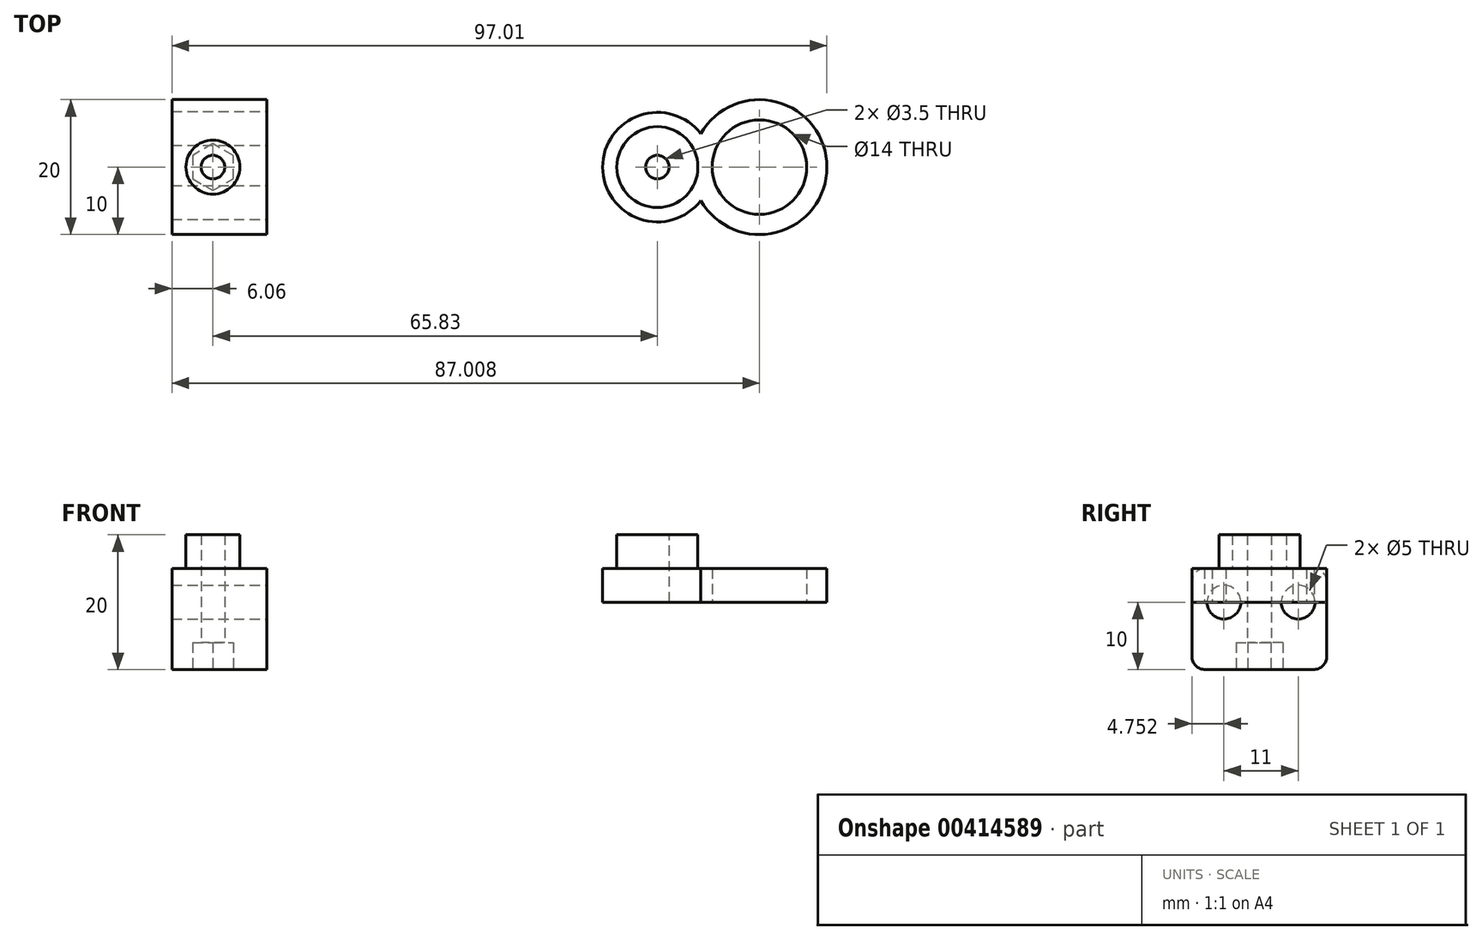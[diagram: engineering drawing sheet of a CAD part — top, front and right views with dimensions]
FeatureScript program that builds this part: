
annotation { "Feature Type Name" : "Feature", "Feature Type Description" : "" }
export const myFeature = defineFeature(function(context is Context, id is Id, definition is map)
    precondition{}
    {
        {
            var Q0;
            Q0=qCreatedBy(makeId("Top.planeOp"),FACE);
            var sketch = newSketch(context, id + "F0", { "sketchPlane" : qUnion([Q0])});
            skCircle(sketch, "E0", {"center": v(15.12, 0) * mm, "radius": 7 * mm});
            skArc(sketch, "E1", {"start": v(6.43, 4.95) * mm, "mid": v(-8.12, 0) * mm, "end": v(6.43, -4.95) * mm});
            skArc(sketch, "E2", {"start": v(6.43, -4.95) * mm, "mid": v(25.12, 0) * mm, "end": v(6.43, 4.95) * mm});
            skCircle(sketch, "E3", {"center": v(0, 0) * mm, "radius": 6 * mm});
            skSolve(sketch);
        }
        {
            var Q0;
            Q0=makeQuery(id+"F0.imprint","IMPRINT",FACE,{"disambiguationData":[TD([[makeQuery(id+"F0.imprint","IMPRINT",EDGE,{"derivedFrom":sQuery(id+"F0.wireOp",EDGE,"E0")}),-1.0]])]});
            extrude(context, id + "F1", {"entities" : qUnion([Q0]), "depth" : 5 * mm});
        }
        {
            var Q0;
            Q0=makeQuery(id+"F0.imprint","IMPRINT",FACE,{"disambiguationData":[TD([[makeQuery(id+"F0.imprint","IMPRINT",EDGE,{"derivedFrom":sQuery(id+"F0.wireOp",EDGE,"E3")}),1.0]])]});
            extrude(context, id + "F2", {"entities" : qUnion([Q0]), "operationType" : NewBodyOperationType.ADD, "depth" : 10 * mm});
        }
        {
            var Q0;
            Q0=makeQuery(id+"F2.opExtrude","CAP_FACE",FACE,{"disambiguationData":[OSD([sQuery(id+"F0.wireOp",EDGE,"E3")])],"isStart":false});
            var sketch = newSketch(context, id + "F3", { "sketchPlane" : qUnion([Q0])});
            skCircle(sketch, "E4", {"center": v(0, 0) * mm, "radius": 1.75 * mm});
            skSolve(sketch);
        }
        {
            var Q0;
            Q0=makeQuery(id+"F3.imprint","IMPRINT",FACE,{"disambiguationData":[TD([[makeQuery(id+"F3.imprint","IMPRINT",EDGE,{"derivedFrom":sQuery(id+"F3.wireOp",EDGE,"E4")}),1.0]])]});
            extrude(context, id + "F4", {"entities" : qUnion([Q0]), "operationType" : NewBodyOperationType.REMOVE, "oppositeDirection" : true, "depth" : 25 * mm});
        }
        {
            var Q0;
            Q0=qCreatedBy(makeId("Top.planeOp"),FACE);
            var sketch = newSketch(context, id + "F5", { "sketchPlane" : qUnion([Q0])});
            skCircle(sketch, "E5", {"center": v(-65.83, 0) * mm, "radius": 1.75 * mm});
            skCircle(sketch, "E6", {"center": v(-65.83, 0) * mm, "radius": 6 * mm});
            skLineSegment(sketch, "E7.bottom", {"start": v(-57.83, 10) * mm, "end": v(-60.83, 10) * mm});
            skLineSegment(sketch, "E7.top", {"start": v(-57.83, -10) * mm, "end": v(-60.83, -10) * mm});
            skLineSegment(sketch, "E7.left", {"start": v(-57.83, 10) * mm, "end": v(-57.83, -10) * mm});
            skLineSegment(sketch, "E7.right", {"start": v(-60.83, 10) * mm, "end": v(-60.83, 3.32) * mm});
            skCircle(sketch, "E8", {"center": v(-65.83, 0) * mm, "radius": 4 * mm});
            skLineSegment(sketch, "E9.trimOffspring", {"start": v(-60.83, -3.32) * mm, "end": v(-60.83, -10) * mm});
            skLineSegment(sketch, "E10.bottom", {"start": v(-60.83, 10) * mm, "end": v(-71.9, 10) * mm});
            skLineSegment(sketch, "E10.top", {"start": v(-60.83, -10) * mm, "end": v(-71.9, -10) * mm});
            skLineSegment(sketch, "E10.left", {"start": v(-60.83, 10) * mm, "end": v(-60.83, -10) * mm});
            skLineSegment(sketch, "E10.right", {"start": v(-71.9, 10) * mm, "end": v(-71.9, -10) * mm});
            skSolve(sketch);
        }
        {
            var Q0;
            Q0=makeQuery(id+"F5.imprint","IMPRINT",FACE,{"disambiguationData":[TD([[makeQuery(id+"F5.imprint","IMPRINT",EDGE,{"derivedFrom":sQuery(id+"F5.wireOp",EDGE,"E6")}),1.0]])]});
            var Q1;
            Q1=makeQuery(id+"F5.imprint","IMPRINT",FACE,{"disambiguationData":[TD([[makeQuery(id+"F5.imprint","IMPRINT",EDGE,{"derivedFrom":sQuery(id+"F5.wireOp",EDGE,"E8")}),-1.0]])]});
            extrude(context, id + "F6", {"entities" : qUnion([Q0, Q1]), "depth" : 5 * mm, "offsetDistance" : 25 * mm, "hasSecondDirection" : true, "secondDirectionOppositeDirection" : true, "secondDirectionDepth" : 10 * mm});
        }
        {
            var Q0;
            Q0=makeQuery(id+"F5.imprint","IMPRINT",FACE,{"disambiguationData":[TD([[makeQuery(id+"F5.imprint","IMPRINT",EDGE,{"derivedFrom":sQuery(id+"F5.wireOp",EDGE,"E5")}),-1.0]])]});
            extrude(context, id + "F7", {"entities" : qUnion([Q0]), "operationType" : NewBodyOperationType.ADD, "depth" : 10 * mm, "offsetDistance" : 25 * mm, "hasSecondDirection" : true, "secondDirectionOppositeDirection" : true, "secondDirectionDepth" : 10 * mm});
        }
        {
            var Q0;
            {var subQ1=sQuery(id+"F5.wireOp",EDGE,"E7.bottom");Q0=makeQuery(id+"F5.imprint","IMPRINT",FACE,{"disambiguationData":[TD([[makeQuery(id+"F5.imprint","IMPRINT",EDGE,{"derivedFrom":subQ1}),1.0]])]});}
            var Q1;
            {var subQ1=sQuery(id+"F5.wireOp",EDGE,"E10.bottom");Q1=makeQuery(id+"F5.imprint","IMPRINT",FACE,{"disambiguationData":[TD([[makeQuery(id+"F5.imprint","IMPRINT",EDGE,{"derivedFrom":subQ1}),1.0]])]});}
            extrude(context, id + "F8", {"entities" : qUnion([Q0, Q1]), "operationType" : NewBodyOperationType.ADD, "depth" : 5 * mm, "offsetDistance" : 25 * mm, "hasSecondDirection" : true, "secondDirectionOppositeDirection" : true, "secondDirectionDepth" : 10 * mm});
        }
        {
            var Q0;
            Q0=makeQuery(id+"F8.opExtrude","SWEPT_FACE",FACE,{"disambiguationData":[OSD([sQuery(id+"F5.wireOp",EDGE,"E7.left")])]});
            var sketch = newSketch(context, id + "F9", { "sketchPlane" : qUnion([Q0])});
            skCircle(sketch, "E11", {"center": v(-5.25, 0) * mm, "radius": 2.5 * mm});
            skCircle(sketch, "E12", {"center": v(5.75, 0) * mm, "radius": 2.5 * mm});
            skSolve(sketch);
        }
        {
            var Q0;
            Q0=makeQuery(id+"F9.imprint","IMPRINT",FACE,{"disambiguationData":[TD([[makeQuery(id+"F9.imprint","IMPRINT",EDGE,{"derivedFrom":sQuery(id+"F9.wireOp",EDGE,"E11")}),1.0]])]});
            var Q1;
            Q1=makeQuery(id+"F9.imprint","IMPRINT",FACE,{"disambiguationData":[TD([[makeQuery(id+"F9.imprint","IMPRINT",EDGE,{"derivedFrom":sQuery(id+"F9.wireOp",EDGE,"E12")}),1.0]])]});
            extrude(context, id + "F10", {"entities" : qUnion([Q0, Q1]), "operationType" : NewBodyOperationType.REMOVE, "oppositeDirection" : true, "depth" : 20 * mm, "offsetDistance" : 25 * mm});
        }
        {
            var Q0;
            Q0=makeQuery(id+"F8.opExtrude","CAP_EDGE",EDGE,{"disambiguationData":[OSD([sQuery(id+"F5.wireOp",EDGE,"E7.top")])],"isStart":false});
            var Q1;
            Q1=makeQuery(id+"F8.opExtrude","CAP_EDGE",EDGE,{"disambiguationData":[OSD([sQuery(id+"F5.wireOp",EDGE,"E7.top")])],"isStart":true});
            var Q2;
            Q2=makeQuery(id+"F8.opExtrude","CAP_EDGE",EDGE,{"disambiguationData":[OSD([sQuery(id+"F5.wireOp",EDGE,"E7.bottom")])],"isStart":false});
            var Q3;
            Q3=makeQuery(id+"F8.opExtrude","CAP_EDGE",EDGE,{"disambiguationData":[OSD([sQuery(id+"F5.wireOp",EDGE,"E7.bottom")])],"isStart":true});
            fillet(context, id + "F11", {"entities" : qUnion([Q0, Q1, Q2, Q3]), "radius" : 2 * mm, "tangentPropagation" : true, "allowEdgeOverflow" : false});
        }
        {
            var Q0;
            {var subQ0=sQuery(id+"F5.wireOp",EDGE,"E6");var subQ1=sQuery(id+"F5.wireOp",EDGE,"E8");Q0=makeQuery(id+"F8.boolean.opBoolean","MERGE",FACE,{"derivedFrom":[makeQuery(id+"F7.boolean.opBoolean","MERGE",FACE,{"derivedFrom":[makeQuery(id+"F6.opExtrude","CAP_FACE",FACE,{"disambiguationData":[OSD([subQ0,subQ1])],"isStart":true}),makeQuery(id+"F7.opExtrude","CAP_FACE",FACE,{"disambiguationData":[OSD([sQuery(id+"F5.wireOp",EDGE,"E5"),subQ1])],"isStart":true})]}),makeQuery(id+"F8.opExtrude","CAP_FACE",FACE,{"disambiguationData":[OSD([subQ0,sQuery(id+"F5.wireOp",EDGE,"E7.bottom"),sQuery(id+"F5.wireOp",EDGE,"E7.top"),sQuery(id+"F5.wireOp",EDGE,"E7.left"),sQuery(id+"F5.wireOp",EDGE,"E10.bottom"),sQuery(id+"F5.wireOp",EDGE,"E10.top"),sQuery(id+"F5.wireOp",EDGE,"E10.right")])],"isStart":true})]});}
            var sketch = newSketch(context, id + "F12", { "sketchPlane" : qUnion([Q0])});
            skCircle(sketch, "E13.cCircle", {"center": v(-65.83, 0) * mm, "radius": 3 * mm, "construction": true});
            skLineSegment(sketch, "E13.0", {"start": v(-62.83, 1.73) * mm, "end": v(-62.83, -1.73) * mm});
            skLineSegment(sketch, "E13.1", {"start": v(-62.83, -1.73) * mm, "end": v(-65.83, -3.46) * mm});
            skLineSegment(sketch, "E13.2", {"start": v(-65.83, -3.46) * mm, "end": v(-68.83, -1.73) * mm});
            skLineSegment(sketch, "E13.3", {"start": v(-68.83, -1.73) * mm, "end": v(-68.83, 1.73) * mm});
            skLineSegment(sketch, "E13.4", {"start": v(-68.83, 1.73) * mm, "end": v(-65.83, 3.46) * mm});
            skLineSegment(sketch, "E13.5", {"start": v(-65.83, 3.46) * mm, "end": v(-62.83, 1.73) * mm});
            skPoint(sketch, "E13.0.midPoint", {"position": v(-62.83, 0) * mm});
            skSolve(sketch);
        }
        {
            var Q0;
            Q0=makeQuery(id+"F12.imprint","IMPRINT",FACE,{"disambiguationData":[TD([[makeQuery(id+"F12.imprint","IMPRINT",EDGE,{"derivedFrom":sQuery(id+"F12.wireOp",EDGE,"E13.0")}),-1.0]])]});
            extrude(context, id + "F13", {"entities" : qUnion([Q0]), "operationType" : NewBodyOperationType.REMOVE, "oppositeDirection" : true, "depth" : 4 * mm, "offsetDistance" : 25 * mm});
        }
    });
